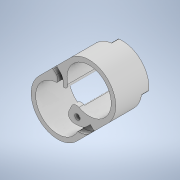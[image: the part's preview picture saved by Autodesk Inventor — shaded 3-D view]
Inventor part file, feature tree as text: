
AUTODESK INVENTOR PART (.ipt)
format: ipt  version: 2020 (Build 240168000, 168)  size: 439,808 bytes
history: native  units: in
note: dims shown in document units (in); Inventor stores cm internally (conversion verified against a paired STEP export)
features: fillet x9, extrude x8, sketch x8, mirror x2
ambient origin geometry x8: Origin, YZ Plane, XZ Plane, XY Plane, X Axis, Y Axis, Z Axis, Center Point
bodies: Solid1 (feature_tree)
feature tree (27):
  extrude  "Extrusion1"  Depth=0.9606in
  extrude  "Extrusion3"  TaperAngle=45.0deg  [1 undecoded]
  extrude  "Extrusion4"  Depth=0.4134in
  extrude  "Extrusion5"  Depth=0.1181in
  fillet  "Fillet1"  Radius=0.1181in
  fillet  "Fillet2"  Radius=0.1181in
  mirror  "Mirror1"
  extrude  "Extrusion6"  Depth=0.9606in
  mirror  "Mirror2"
  fillet  "Fillet3"  Radius=0.1772in
  extrude  "Extrusion8"  Depth=0.6102in TaperAngle=0.0deg
  extrude  "Extrusion11"  Depth=0.0787in TaperAngle=0.0deg
  fillet  "Fillet8"  Radius=0.5787in
  fillet  "Fillet10"  Radius=0.5787in
  fillet  "Fillet11"  Radius=1.1575in
  fillet  "Fillet12"  Radius=0.5787in
  extrude  "Extrusion12"  Depth=0.7185in TaperAngle=0.0deg
  fillet  "Fillet13"  Radius=0.1181in
  fillet  "Fillet14"  Radius=0.1181in
  sketch  "Sketch1"  dims[d0=0.9724in d1=0.9606in]
  sketch  "Sketch6"  dims[d24=0.9606in d25=0.9606in d26=0.1772in]
  sketch  "Sketch9"  dims[d27=0.1083in d28=0.0in]
  sketch  "Sketch12"  dims[d32=0.9724in d33=0.9606in d34=0.0in d35=45.0deg d36=0.0in d37=0.4134in d38=0.3346in d39=0.1181in d40=0.1181in d41=0.1181in d42=0.9606in d43=0.9606in d44=0.1772in d45=0.6102in d46=0.0in]
  sketch  "Sketch13"  dims[d49=0.2165in d50=0.0787in d51=0.0394in d52=0.0in d53=0.0in d54=0.9724in d55=0.9606in d56=0.0in d57=45.0deg d58=0.0in d59=0.4134in d60=0.3346in d61=0.1181in d62=0.1181in d63=0.1181in d64=0.9606in d65=0.9606in d66=0.1772in d67=0.5787in d68=0.5787in d69=1.1575in d70=0.5787in d71=0.7185in d72=0.0in d73=0.1181in d74=0.1181in d75=0.7185in d76=0.0in d77=0.0787in d92=0.1181in d93=0.0in d112=0.1181in d113=0.1181in d114=0.0in d115=0.0in d116=0.9843in d117=0.9843in d118=1.9685in d119=1.9685in d120=0.1181in d121=0.0in d123=0.0394in d125=0.0197in d126=0.0197in d127=0.0197in d130=0.1181in d131=0.1181in d132=0.0in d134=0.0in d135=0.1181in d136=0.1181in d137=0.0in d138=0.1181in d140=0.0086in d141=0.2362in d142=0.0591in d143=0.7087in d144=0.0in d145=0.0197in d146=0.0197in d78=0.0344in]
  sketch  "Sketch3"  dims[d2=0.0in d3=45.0deg]
  sketch  "Sketch4"  dims[d4=0.0in d5=0.4134in]
  sketch  "Sketch5"  dims[d20=0.3346in d21=0.1181in d22=0.1181in d23=0.1181in]
note: 1 required parameter value undecoded (feature->parameter linkage not recoverable at this tier; creation-order binding heuristic only, values carry confidence <= 0.55)
